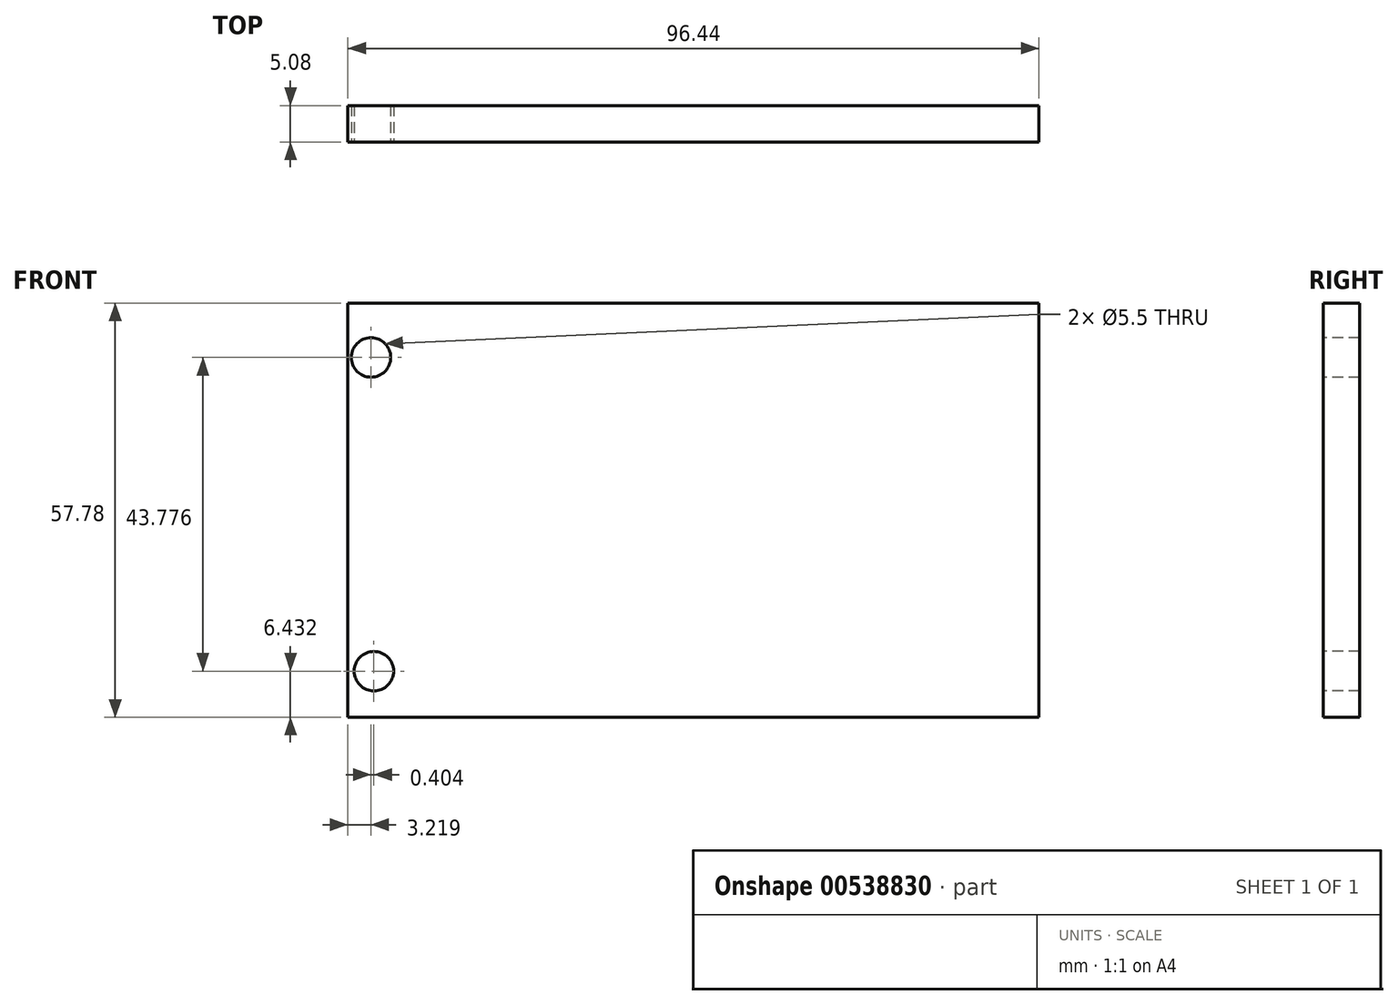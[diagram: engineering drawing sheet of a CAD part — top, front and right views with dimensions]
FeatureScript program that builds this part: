
annotation { "Feature Type Name" : "Feature", "Feature Type Description" : "" }
export const myFeature = defineFeature(function(context is Context, id is Id, definition is map)
    precondition{}
    {
        {
            var Q0;
            Q0=qCreatedBy(makeId("Front.planeOp"),FACE);
            var sketch = newSketch(context, id + "F0", { "sketchPlane" : qUnion([Q0])});
            skLineSegment(sketch, "E0.bottom", {"start": v(-48.22, 28.9) * mm, "end": v(48.22, 28.9) * mm});
            skLineSegment(sketch, "E0.top", {"start": v(-48.22, -28.9) * mm, "end": v(48.22, -28.9) * mm});
            skLineSegment(sketch, "E0.left", {"start": v(-48.22, 28.9) * mm, "end": v(-48.22, -28.9) * mm});
            skLineSegment(sketch, "E0.right", {"start": v(48.22, 28.9) * mm, "end": v(48.22, -28.9) * mm});
            skPoint(sketch, "E0.middle", {"position": v(0, 0) * mm});
            skSolve(sketch);
        }
        {
            var Q0;
            Q0=makeQuery(id+"F0.imprint","IMPRINT",FACE,{"disambiguationData":[TD([[makeQuery(id+"F0.imprint","IMPRINT",EDGE,{"derivedFrom":sQuery(id+"F0.wireOp",EDGE,"E0.bottom")}),-1.0]])]});
            extrude(context, id + "F1", {"entities" : qUnion([Q0]), "depth" : 5.08 * mm, "offsetDistance" : 25.4 * mm});
        }
        {
            var Q0;
            Q0=makeQuery(id+"F1.opExtrude","CAP_FACE",FACE,{"disambiguationData":[OSD([sQuery(id+"F0.wireOp",EDGE,"E0.bottom"),sQuery(id+"F0.wireOp",EDGE,"E0.top"),sQuery(id+"F0.wireOp",EDGE,"E0.left"),sQuery(id+"F0.wireOp",EDGE,"E0.right")])],"isStart":false});
            var sketch = newSketch(context, id + "F2", { "sketchPlane" : qUnion([Q0])});
            skCircle(sketch, "E1", {"center": v(-45, 21.32) * mm, "radius": 1.15 * mm});
            skCircle(sketch, "E2", {"center": v(-44.6, -22.46) * mm, "radius": 1.45 * mm});
            skSolve(sketch);
        }
        {
            var Q0;
            Q0=sQuery(id+"F2.wireOp",VERTEX,"E1.center");
            var Q1;
            Q1=sQuery(id+"F2.wireOp",VERTEX,"E2.center");
            var Q2;
            Q2=makeQuery(id+"F1.opExtrude","SWEPT_BODY",BODY,{"disambiguationData":[OSD([sQuery(id+"F0.wireOp",EDGE,"E0.bottom"),sQuery(id+"F0.wireOp",EDGE,"E0.top"),sQuery(id+"F0.wireOp",EDGE,"E0.left"),sQuery(id+"F0.wireOp",EDGE,"E0.right")])]});
            hole(context, id + "F3", {"style" : HoleStyle.SIMPLE, "endStyle" : HoleEndStyle.THROUGH, "standardTappedOrClearance" : lookupTablePath({ "standard" : "ISO", "fit" : "Normal", "size" : "M5", "type" : "Clearance" }), "standardBlindInLast" : lookupTablePath({ "fit" : "Standard", "standard" : "ISO", "size" : "M5", "type" : "Clearance" }), "holeDiameter" : 5.5 * mm, "isTappedThrough" : true, "tappedDepth" : 12.7 * mm, "tapClearance" : 3, "locations" : qUnion([Q0, Q1]), "scope" : qUnion([Q2])});
        }
    });
